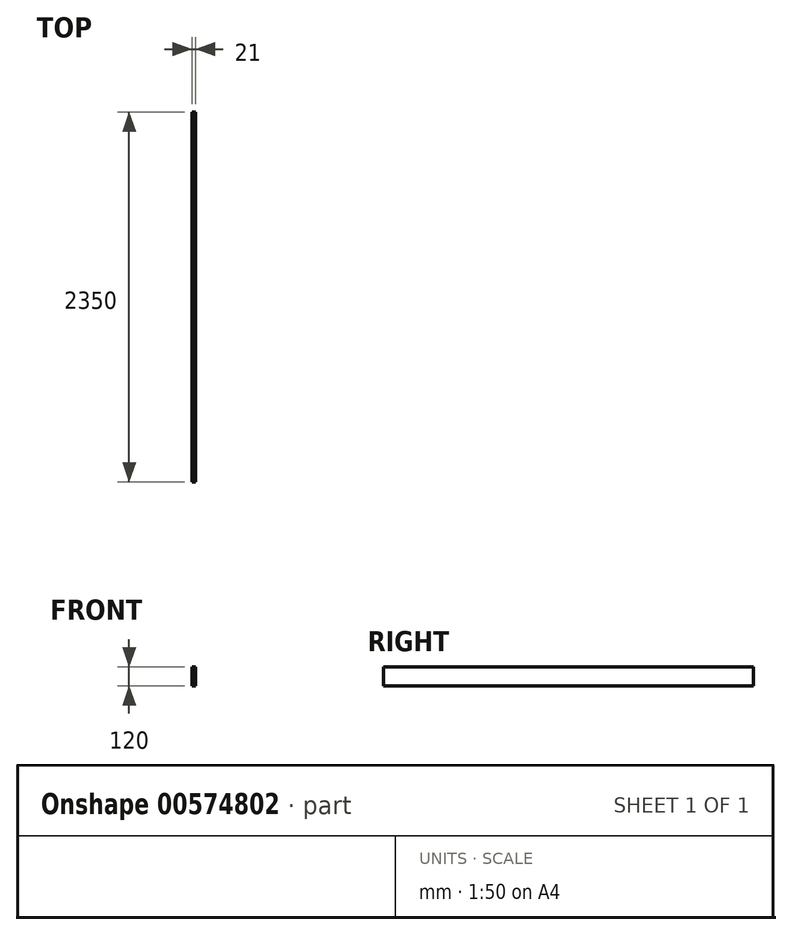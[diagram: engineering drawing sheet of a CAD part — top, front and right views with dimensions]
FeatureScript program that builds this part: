
annotation { "Feature Type Name" : "Feature", "Feature Type Description" : "" }
export const myFeature = defineFeature(function(context is Context, id is Id, definition is map)
    precondition{}
    {
        {
            var Q0;
            Q0=qCreatedBy(makeId("Front.planeOp"),FACE);
            var sketch = newSketch(context, id + "F0", { "sketchPlane" : qUnion([Q0])});
            skLineSegment(sketch, "E0.bottom", {"start": v(-10.5, 60) * mm, "end": v(10.5, 60) * mm});
            skLineSegment(sketch, "E0.top", {"start": v(-10.5, -60) * mm, "end": v(10.5, -60) * mm});
            skLineSegment(sketch, "E0.left", {"start": v(-10.5, 60) * mm, "end": v(-10.5, -60) * mm});
            skLineSegment(sketch, "E0.right", {"start": v(10.5, 60) * mm, "end": v(10.5, -60) * mm});
            skSolve(sketch);
        }
        {
            var Q0;
            Q0=qSketchRegion(id+"F0",true);
            extrude(context, id + "F1", {"entities" : qUnion([Q0]), "depth" : 2350 * mm, "offsetDistance" : 25 * mm});
        }
    });
